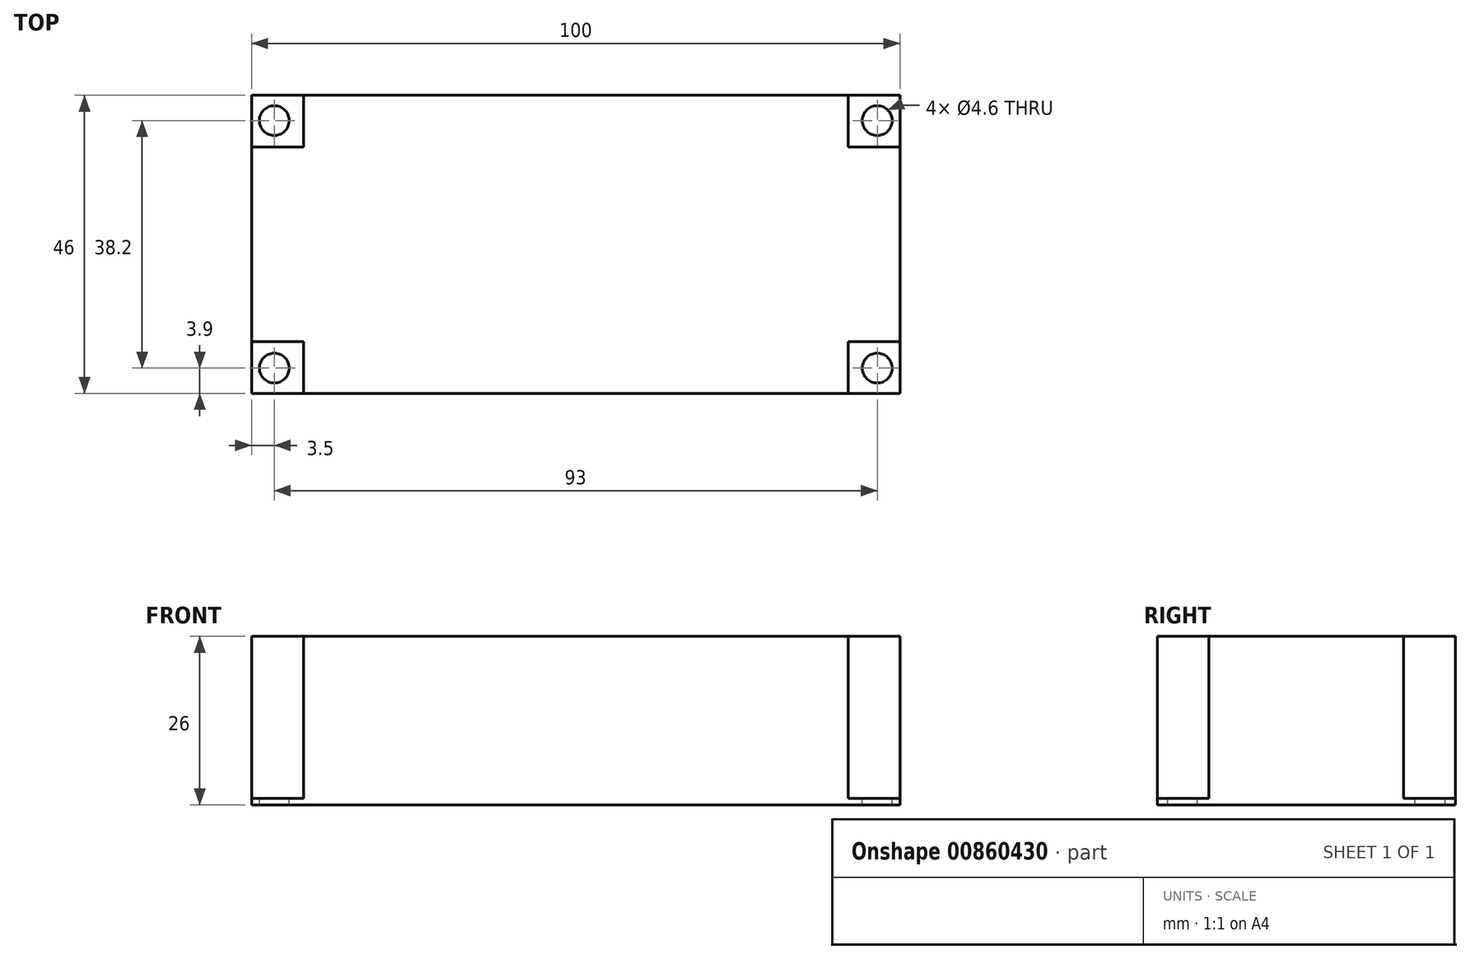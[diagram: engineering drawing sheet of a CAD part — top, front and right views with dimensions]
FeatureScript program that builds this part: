
annotation { "Feature Type Name" : "Feature", "Feature Type Description" : "" }
export const myFeature = defineFeature(function(context is Context, id is Id, definition is map)
    precondition{}
    {
        {
            var Q0;
            Q0=qCreatedBy(makeId("Top.planeOp"),FACE);
            var sketch = newSketch(context, id + "F0", { "sketchPlane" : qUnion([Q0])});
            skLineSegment(sketch, "E0.bottom", {"start": v(-50, 23) * mm, "end": v(50, 23) * mm});
            skLineSegment(sketch, "E0.top", {"start": v(-50, -23) * mm, "end": v(50, -23) * mm});
            skLineSegment(sketch, "E0.left", {"start": v(-50, 23) * mm, "end": v(-50, -23) * mm});
            skLineSegment(sketch, "E0.right", {"start": v(50, 23) * mm, "end": v(50, -23) * mm});
            skLineSegment(sketch, "E1.bottom", {"start": v(-50, 23) * mm, "end": v(-42, 23) * mm});
            skLineSegment(sketch, "E1.top", {"start": v(-50, 15) * mm, "end": v(-42, 15) * mm});
            skLineSegment(sketch, "E1.left", {"start": v(-50, 23) * mm, "end": v(-50, 15) * mm});
            skLineSegment(sketch, "E1.right", {"start": v(-42, 23) * mm, "end": v(-42, 15) * mm});
            skLineSegment(sketch, "E2.bottom", {"start": v(50, 23) * mm, "end": v(42, 23) * mm});
            skLineSegment(sketch, "E2.top", {"start": v(50, 15) * mm, "end": v(42, 15) * mm});
            skLineSegment(sketch, "E2.left", {"start": v(50, 23) * mm, "end": v(50, 15) * mm});
            skLineSegment(sketch, "E2.right", {"start": v(42, 23) * mm, "end": v(42, 15) * mm});
            skLineSegment(sketch, "E3.bottom", {"start": v(50, -23) * mm, "end": v(42, -23) * mm});
            skLineSegment(sketch, "E3.top", {"start": v(50, -15) * mm, "end": v(42, -15) * mm});
            skLineSegment(sketch, "E3.left", {"start": v(50, -23) * mm, "end": v(50, -15) * mm});
            skLineSegment(sketch, "E3.right", {"start": v(42, -23) * mm, "end": v(42, -15) * mm});
            skLineSegment(sketch, "E4.bottom", {"start": v(-50, -23) * mm, "end": v(-42, -23) * mm});
            skLineSegment(sketch, "E4.top", {"start": v(-50, -15) * mm, "end": v(-42, -15) * mm});
            skLineSegment(sketch, "E4.left", {"start": v(-50, -23) * mm, "end": v(-50, -15) * mm});
            skLineSegment(sketch, "E4.right", {"start": v(-42, -23) * mm, "end": v(-42, -15) * mm});
            skSolve(sketch);
        }
        {
            var Q0;
            {var subQ3=sQuery(id+"F0.wireOp",EDGE,"E1.top");Q0=makeQuery(id+"F0.imprint","IMPRINT",FACE,{"disambiguationData":[TD([[makeQuery(id+"F0.imprint","IMPRINT",EDGE,{"derivedFrom":subQ3}),-1.0]])]});}
            extrude(context, id + "F1", {"entities" : qUnion([Q0]), "depth" : 25 * mm, "offsetDistance" : 25 * mm});
        }
        {
            var Q0;
            {var subQ4=sQuery(id+"F0.wireOp",EDGE,"E4.top");Q0=makeQuery(id+"F0.imprint","IMPRINT",FACE,{"disambiguationData":[TD([[makeQuery(id+"F0.imprint","IMPRINT",EDGE,{"derivedFrom":subQ4}),-1.0]])]});}
            var Q1;
            {var subQ4=sQuery(id+"F0.wireOp",EDGE,"E1.top");Q1=makeQuery(id+"F0.imprint","IMPRINT",FACE,{"disambiguationData":[TD([[makeQuery(id+"F0.imprint","IMPRINT",EDGE,{"derivedFrom":subQ4}),1.0]])]});}
            var Q2;
            {var subQ4=sQuery(id+"F0.wireOp",EDGE,"E2.top");Q2=makeQuery(id+"F0.imprint","IMPRINT",FACE,{"disambiguationData":[TD([[makeQuery(id+"F0.imprint","IMPRINT",EDGE,{"derivedFrom":subQ4}),-1.0]])]});}
            var Q3;
            {var subQ4=sQuery(id+"F0.wireOp",EDGE,"E3.top");Q3=makeQuery(id+"F0.imprint","IMPRINT",FACE,{"disambiguationData":[TD([[makeQuery(id+"F0.imprint","IMPRINT",EDGE,{"derivedFrom":subQ4}),1.0]])]});}
            var Q4;
            {var subQ3=sQuery(id+"F0.wireOp",EDGE,"E1.top");Q4=makeQuery(id+"F0.imprint","IMPRINT",FACE,{"disambiguationData":[TD([[makeQuery(id+"F0.imprint","IMPRINT",EDGE,{"derivedFrom":subQ3}),-1.0]])]});}
            extrude(context, id + "F2", {"entities" : qUnion([Q0, Q1, Q2, Q3, Q4]), "operationType" : NewBodyOperationType.ADD, "oppositeDirection" : true, "depth" : 1 * mm, "offsetDistance" : 25 * mm});
        }
        {
            var Q0;
            Q0=qCreatedBy(makeId("Top.planeOp"),FACE);
            var sketch = newSketch(context, id + "F3", { "sketchPlane" : qUnion([Q0])});
            skCircle(sketch, "E5", {"center": v(-46.5, -19.1) * mm, "radius": 2.3 * mm});
            skCircle(sketch, "E6", {"center": v(46.5, -19.1) * mm, "radius": 2.3 * mm});
            skCircle(sketch, "E7", {"center": v(46.5, 19.1) * mm, "radius": 2.3 * mm});
            skCircle(sketch, "E8", {"center": v(-46.5, 19.1) * mm, "radius": 2.3 * mm});
            skSolve(sketch);
        }
        {
            var Q0;
            Q0=makeQuery(id+"F3.imprint","IMPRINT",FACE,{"disambiguationData":[TD([[makeQuery(id+"F3.imprint","IMPRINT",EDGE,{"derivedFrom":sQuery(id+"F3.wireOp",EDGE,"E5")}),1.0]])]});
            var Q1;
            Q1=makeQuery(id+"F3.imprint","IMPRINT",FACE,{"disambiguationData":[TD([[makeQuery(id+"F3.imprint","IMPRINT",EDGE,{"derivedFrom":sQuery(id+"F3.wireOp",EDGE,"E6")}),1.0]])]});
            var Q2;
            Q2=makeQuery(id+"F3.imprint","IMPRINT",FACE,{"disambiguationData":[TD([[makeQuery(id+"F3.imprint","IMPRINT",EDGE,{"derivedFrom":sQuery(id+"F3.wireOp",EDGE,"E8")}),1.0]])]});
            var Q3;
            Q3=makeQuery(id+"F3.imprint","IMPRINT",FACE,{"disambiguationData":[TD([[makeQuery(id+"F3.imprint","IMPRINT",EDGE,{"derivedFrom":sQuery(id+"F3.wireOp",EDGE,"E7")}),1.0]])]});
            extrude(context, id + "F4", {"entities" : qUnion([Q0, Q1, Q2, Q3]), "operationType" : NewBodyOperationType.REMOVE, "oppositeDirection" : true, "depth" : 25 * mm, "offsetDistance" : 25 * mm});
        }
    });
